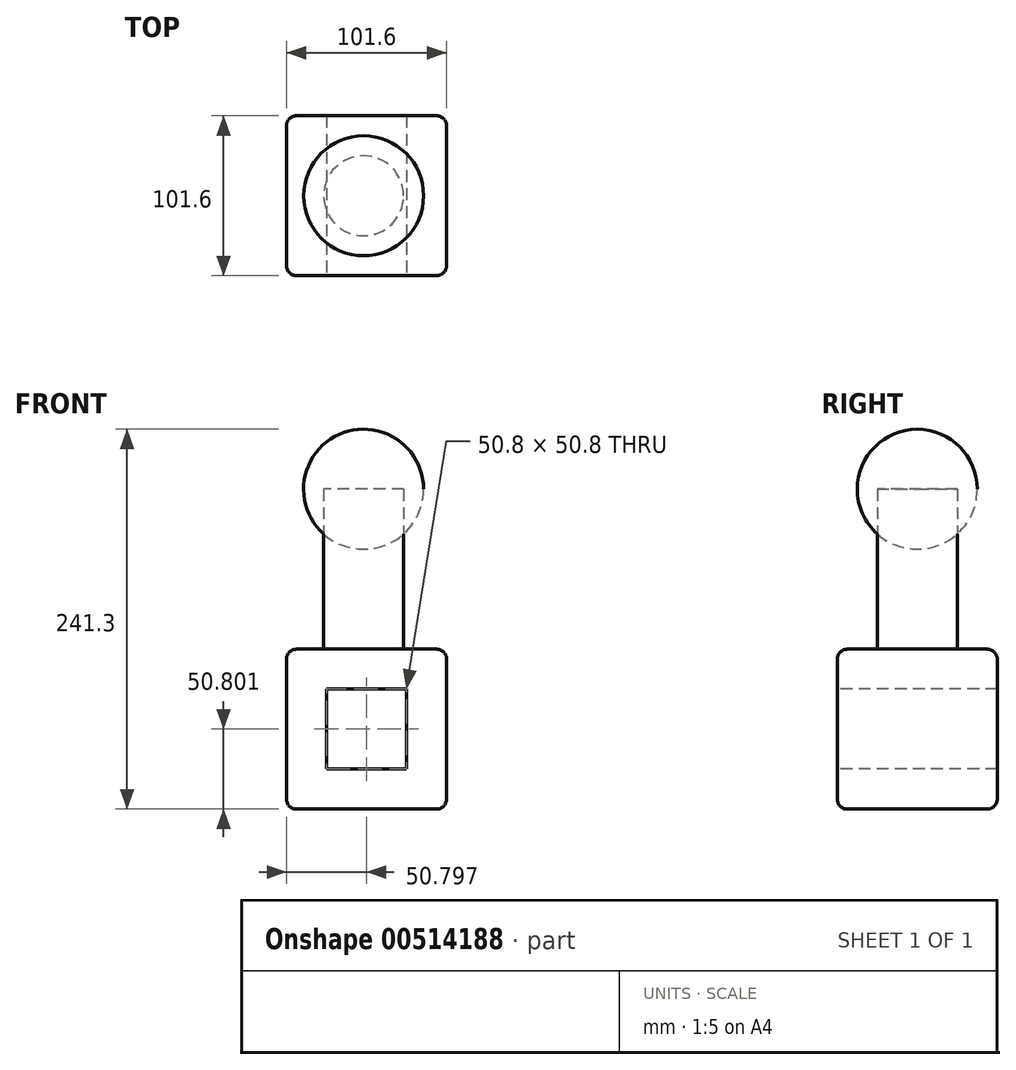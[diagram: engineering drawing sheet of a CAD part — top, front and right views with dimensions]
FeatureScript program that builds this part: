
annotation { "Feature Type Name" : "Feature", "Feature Type Description" : "" }
export const myFeature = defineFeature(function(context is Context, id is Id, definition is map)
    precondition{}
    {
        {
            var Q0;
            Q0=qCreatedBy(makeId("Front.planeOp"),FACE);
            var sketch = newSketch(context, id + "F0", { "sketchPlane" : qUnion([Q0])});
            skLineSegment(sketch, "E0.bottom", {"start": v(-48.94, 57.36) * mm, "end": v(52.66, 57.36) * mm});
            skLineSegment(sketch, "E0.top", {"start": v(-48.94, -44.24) * mm, "end": v(52.66, -44.24) * mm});
            skLineSegment(sketch, "E0.left", {"start": v(-48.94, 57.36) * mm, "end": v(-48.94, -44.24) * mm});
            skLineSegment(sketch, "E0.right", {"start": v(52.66, 57.36) * mm, "end": v(52.66, -44.24) * mm});
            skSolve(sketch);
        }
        {
            var Q0;
            Q0=makeQuery(id+"F0.imprint","IMPRINT",FACE,{"disambiguationData":[TD([[makeQuery(id+"F0.imprint","IMPRINT",EDGE,{"derivedFrom":sQuery(id+"F0.wireOp",EDGE,"E0.bottom")}),-1.0]])]});
            extrude(context, id + "F1", {"entities" : qUnion([Q0]), "depth" : 101.6 * mm});
        }
        {
            var Q0;
            Q0=makeQuery(id+"F1.opExtrude","SWEPT_FACE",FACE,{"disambiguationData":[OSD([sQuery(id+"F0.wireOp",EDGE,"E0.bottom")])]});
            var sketch = newSketch(context, id + "F2", { "sketchPlane" : qUnion([Q0])});
            skCircle(sketch, "E1", {"center": v(0, -50.8) * mm, "radius": 25.4 * mm});
            skPoint(sketch, "E1.centerSnap0", {"position": v(-48.94, -50.8) * mm});
            skSolve(sketch);
        }
        {
            var Q0;
            Q0=makeQuery(id+"F2.imprint","IMPRINT",FACE,{"disambiguationData":[TD([[makeQuery(id+"F2.imprint","IMPRINT",EDGE,{"derivedFrom":sQuery(id+"F2.wireOp",EDGE,"J8tDwDtn-UGIa-uK9W-E3up-PdiTtbVAndhc")}),1.0]])]});
            var Q1;
            Q1=makeQuery(id+"F2.imprint","IMPRINT",FACE,{"disambiguationData":[TD([[makeQuery(id+"F2.imprint","IMPRINT",EDGE,{"derivedFrom":sQuery(id+"F2.wireOp",EDGE,"E1")}),1.0]])]});
            extrude(context, id + "F3", {"entities" : qUnion([Q0, Q1]), "operationType" : NewBodyOperationType.ADD, "depth" : 101.6 * mm});
        }
        {
            var Q0;
            Q0=makeQuery(id+"F3.opExtrude","CAP_FACE",FACE,{"disambiguationData":[OSD([sQuery(id+"F2.wireOp",EDGE,"E1")])],"isStart":false});
            var sketch = newSketch(context, id + "F4", { "sketchPlane" : qUnion([Q0])});
            skCircle(sketch, "E2", {"center": v(0, -50.8) * mm, "radius": 38.1 * mm});
            skLineSegment(sketch, "E3", {"start": v(0, -12.7) * mm, "end": v(0, -88.9) * mm});
            skSolve(sketch);
        }
        {
            var Q0;
            {var subQ0=sQuery(id+"F4.wireOp",EDGE,"E3");var subQ1=sQuery(id+"F4.wireOp",EDGE,"E2");var subQ2=makeQuery(id+"F4.imprint","INTERSECT",VERTEX,{"disambiguationData":[OD(0.0)],"derivedFrom":[subQ1,subQ0]});Q0=makeQuery(id+"F4.imprint","IMPRINT",FACE,{"disambiguationData":[TD([[makeQuery(id+"F4.imprint","IMPRINT",EDGE,{"disambiguationData":[TD([[subQ2,-1.0]])],"derivedFrom":subQ1}),1.0]])]});}
            var Q1;
            {var subQ0=sQuery(id+"F4.wireOp",EDGE,"E3");var subQ1=makeQuery(id+"F3.opExtrude","CAP_EDGE",EDGE,{"disambiguationData":[OSD([sQuery(id+"F2.wireOp",EDGE,"E1")])],"isStart":false});var subQ2=makeQuery(id+"F4.imprint","INTERSECT",VERTEX,{"disambiguationData":[OD(0.0)],"derivedFrom":[subQ1,subQ0]});Q1=makeQuery(id+"F4.imprint","IMPRINT",FACE,{"disambiguationData":[TD([[makeQuery(id+"F4.imprint","IMPRINT",EDGE,{"disambiguationData":[TD([[subQ2,-1.0]])],"derivedFrom":subQ0}),-1.0]])]});}
            var Q2;
            Q2=sQuery(id+"F4.wireOp",EDGE,"E3");
            revolve(context, id + "F5", {"entities" : qUnion([Q0, Q1]), "axis" : qUnion([Q2]), "revolveType" : RevolveType.FULL});
        }
        {
            var Q0;
            Q0=makeQuery(id+"F1.opExtrude","CAP_FACE",FACE,{"disambiguationData":[OSD([sQuery(id+"F0.wireOp",EDGE,"E0.bottom"),sQuery(id+"F0.wireOp",EDGE,"E0.top"),sQuery(id+"F0.wireOp",EDGE,"E0.left"),sQuery(id+"F0.wireOp",EDGE,"E0.right")])],"isStart":false});
            var sketch = newSketch(context, id + "F6", { "sketchPlane" : qUnion([Q0])});
            skLineSegment(sketch, "E4.bottom", {"start": v(-23.54, 31.96) * mm, "end": v(27.26, 31.96) * mm});
            skLineSegment(sketch, "E4.top", {"start": v(-23.54, -18.84) * mm, "end": v(27.26, -18.84) * mm});
            skLineSegment(sketch, "E4.left", {"start": v(-23.54, 31.96) * mm, "end": v(-23.54, -18.84) * mm});
            skLineSegment(sketch, "E4.right", {"start": v(27.26, 31.96) * mm, "end": v(27.26, -18.84) * mm});
            skPoint(sketch, "E4.middle", {"position": v(1.86, 6.56) * mm});
            skPoint(sketch, "E4.middle.positionSnap0", {"position": v(52.66, 6.56) * mm});
            skPoint(sketch, "E4.middle.positionSnap1", {"position": v(1.86, 57.36) * mm});
            skPoint(sketch, "E4.centerSnap0", {"position": v(52.66, 6.56) * mm});
            skPoint(sketch, "E4.centerSnap1", {"position": v(1.86, 57.36) * mm});
            skSolve(sketch);
        }
        {
            var Q0;
            Q0=makeQuery(id+"F6.imprint","IMPRINT",FACE,{"disambiguationData":[TD([[makeQuery(id+"F6.imprint","IMPRINT",EDGE,{"derivedFrom":sQuery(id+"F6.wireOp",EDGE,"E4.bottom")}),-1.0]])]});
            extrude(context, id + "F7", {"entities" : qUnion([Q0]), "operationType" : NewBodyOperationType.REMOVE, "oppositeDirection" : true, "depth" : 101.6 * mm});
        }
        {
            var Q0;
            Q0=makeQuery(id+"F1.opExtrude","CAP_EDGE",EDGE,{"disambiguationData":[OSD([sQuery(id+"F0.wireOp",EDGE,"E0.bottom")])],"isStart":false});
            var Q1;
            Q1=makeQuery(id+"F1.opExtrude","CAP_EDGE",EDGE,{"disambiguationData":[OSD([sQuery(id+"F0.wireOp",EDGE,"E0.right")])],"isStart":false});
            var Q2;
            Q2=makeQuery(id+"F1.opExtrude","CAP_EDGE",EDGE,{"disambiguationData":[OSD([sQuery(id+"F0.wireOp",EDGE,"E0.top")])],"isStart":false});
            var Q3;
            Q3=makeQuery(id+"F1.opExtrude","CAP_EDGE",EDGE,{"disambiguationData":[OSD([sQuery(id+"F0.wireOp",EDGE,"E0.left")])],"isStart":false});
            var Q4;
            Q4=makeQuery(id+"F1.opExtrude","SWEPT_EDGE",EDGE,{"disambiguationData":[OSD([sQuery(id+"F0.wireOp",EDGE,"E0.bottom"),sQuery(id+"F0.wireOp",EDGE,"E0.left")])]});
            var Q5;
            Q5=makeQuery(id+"F1.opExtrude","CAP_EDGE",EDGE,{"disambiguationData":[OSD([sQuery(id+"F0.wireOp",EDGE,"E0.bottom")])],"isStart":true});
            var Q6;
            Q6=makeQuery(id+"F1.opExtrude","SWEPT_EDGE",EDGE,{"disambiguationData":[OSD([sQuery(id+"F0.wireOp",EDGE,"E0.bottom"),sQuery(id+"F0.wireOp",EDGE,"E0.right")])]});
            var Q7;
            Q7=makeQuery(id+"F1.opExtrude","SWEPT_EDGE",EDGE,{"disambiguationData":[OSD([sQuery(id+"F0.wireOp",EDGE,"E0.top"),sQuery(id+"F0.wireOp",EDGE,"E0.right")])]});
            var Q8;
            Q8=makeQuery(id+"F1.opExtrude","CAP_EDGE",EDGE,{"disambiguationData":[OSD([sQuery(id+"F0.wireOp",EDGE,"E0.right")])],"isStart":true});
            var Q9;
            Q9=makeQuery(id+"F1.opExtrude","CAP_EDGE",EDGE,{"disambiguationData":[OSD([sQuery(id+"F0.wireOp",EDGE,"E0.top")])],"isStart":true});
            var Q10;
            Q10=makeQuery(id+"F1.opExtrude","SWEPT_EDGE",EDGE,{"disambiguationData":[OSD([sQuery(id+"F0.wireOp",EDGE,"E0.top"),sQuery(id+"F0.wireOp",EDGE,"E0.left")])]});
            var Q11;
            Q11=makeQuery(id+"F1.opExtrude","CAP_EDGE",EDGE,{"disambiguationData":[OSD([sQuery(id+"F0.wireOp",EDGE,"E0.left")])],"isStart":true});
            fillet(context, id + "F8", {"entities" : qUnion([Q0, Q1, Q2, Q3, Q4, Q5, Q6, Q7, Q8, Q9, Q10, Q11]), "radius" : 6.35 * mm, "tangentPropagation" : true, "allowEdgeOverflow" : false});
        }
    });
